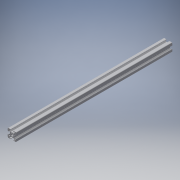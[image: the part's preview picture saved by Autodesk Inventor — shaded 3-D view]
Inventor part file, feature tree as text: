
AUTODESK INVENTOR PART (.ipt)
format: ipt  version: 2016 (Build 200138000, 138)  size: 315,904 bytes
history: native  units: in
note: dims shown in document units (in); Inventor stores cm internally (conversion verified against a paired STEP export)
features: other x3, extrude x1, sketch x1
ambient origin geometry x8: Origin, YZ Plane, XZ Plane, XY Plane, X Axis, Y Axis, Z Axis, Center Point
bodies: Solid1 (feature_tree)
feature tree (5):
  other  "Blocks"
  extrude  "Extrusion1"  [1 undecoded]
  sketch  "Sketch1"  dims[d1=0.0in]
  other  "20x20"
  other  "20x20:1"
note: 1 required parameter value undecoded (feature->parameter linkage not recoverable at this tier; creation-order binding heuristic only, values carry confidence <= 0.55)
